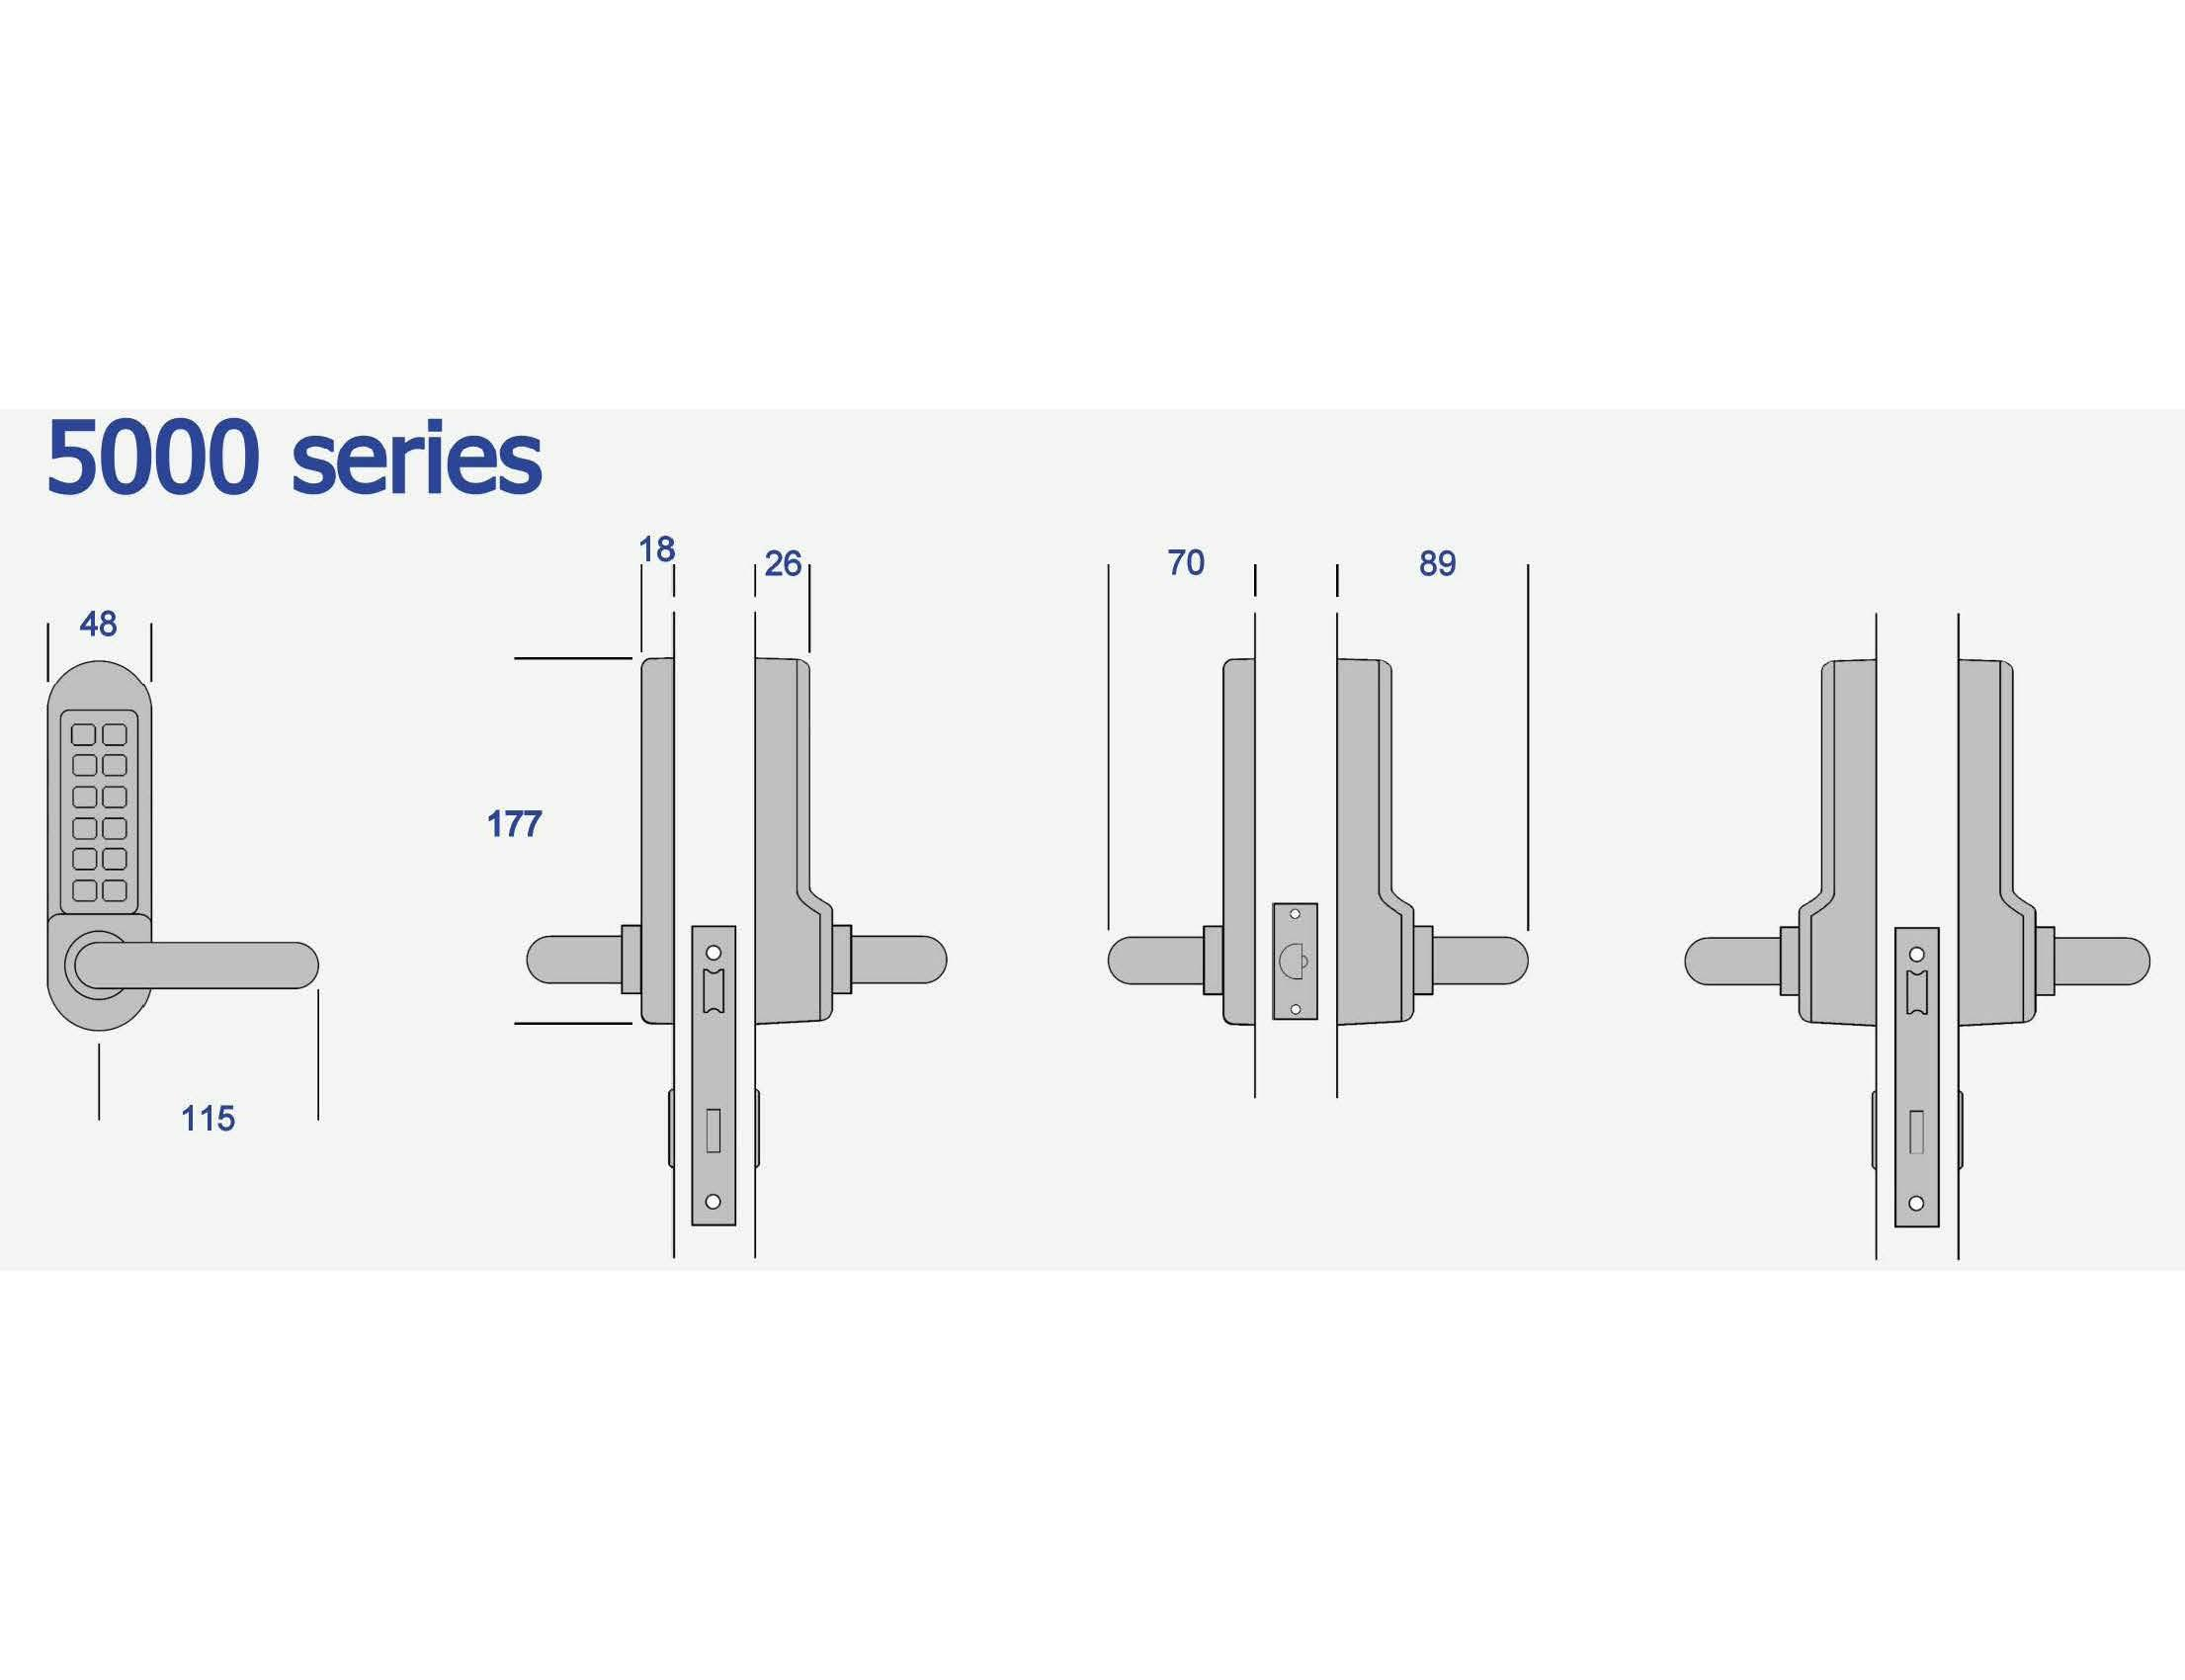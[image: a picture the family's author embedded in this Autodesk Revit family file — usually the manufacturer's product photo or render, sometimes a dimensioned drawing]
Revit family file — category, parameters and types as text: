
# Revit family: NBS_Lomax_Door_FDIN24-24S
name_source: partatom
category: Doors
revit_build: Autodesk Revit Architecture 2016 (Build: 20150220_1215(x64)
units: mm (PartAtom-declared; Revit-internal decimal feet)

## family parameters
Always vertical = Yes
Cut with Voids When Loaded = No
Host = Wall
OmniClass Number = 23.30.10.00
OmniClass Title = Doors
Room Calculation Point = No
Shared = No

## types (1)
- NBS_Lomax_Door_FDIN24-24S
    BIMObjectName = NBS_Lomax_Door_FDIN24-24S
    Category = Doors
    Description = French Doors
    Frame Projection Ext. = 25 mm  [stored 0.082021 ft]
    Frame Projection Int. = 25 mm  [stored 0.082021 ft]
    Frame Width = 76 mm
    Function = Interior
    Glass = Glass
    Height = 2240 mm  [stored 7.34908 ft]
    Higes = Yes
    Hinges = Yes
    Lever Height from FFL = 1000 mm  [stored 3.28084 ft]
    Manufacturer = Lomax
    ManufacturerName = Lomax
    ManufacturerURL = lomaxwood.co.uk
    Model = NBS_Lomax_Door_FDIN24-24S
    ModelNumber = FDIN24-24S
    ModelReference = NBS_Lomax_Door_FDIN24-24S
    NBSDescription = French Doors
    NBSNote = FDIN24-24S
    NBSReference = NBS_Lomax_Door_FDIN24-24S
    Name = FDIN24-24S
    NominalHeight = 2240 mm  [stored 7.34908 ft]
    NominalLength = 76 mm
    NominalWidth = 1480 mm  [stored 4.85564 ft]
    ProductInformation = French Doors
    Revision = 1
    Rough Height = 2240 mm  [stored 7.34908 ft]
    Rough Width = 620 mm
    Thickness = 76 mm
    URL = lomaxwood.co.uk
    Wall Closure = By host
    White = White
    White Wood = WHite Wood
    Width = 1480 mm  [stored 4.85564 ft]
    Wood Wood = Wood Wood

note: [stored X ft] marks values corroborated as IEEE doubles in the binary element streams (Revit-internal decimal feet)

## geometry (parser evidence)
native form markers: Sweep x18
no freeform markers — native parametric forms only
